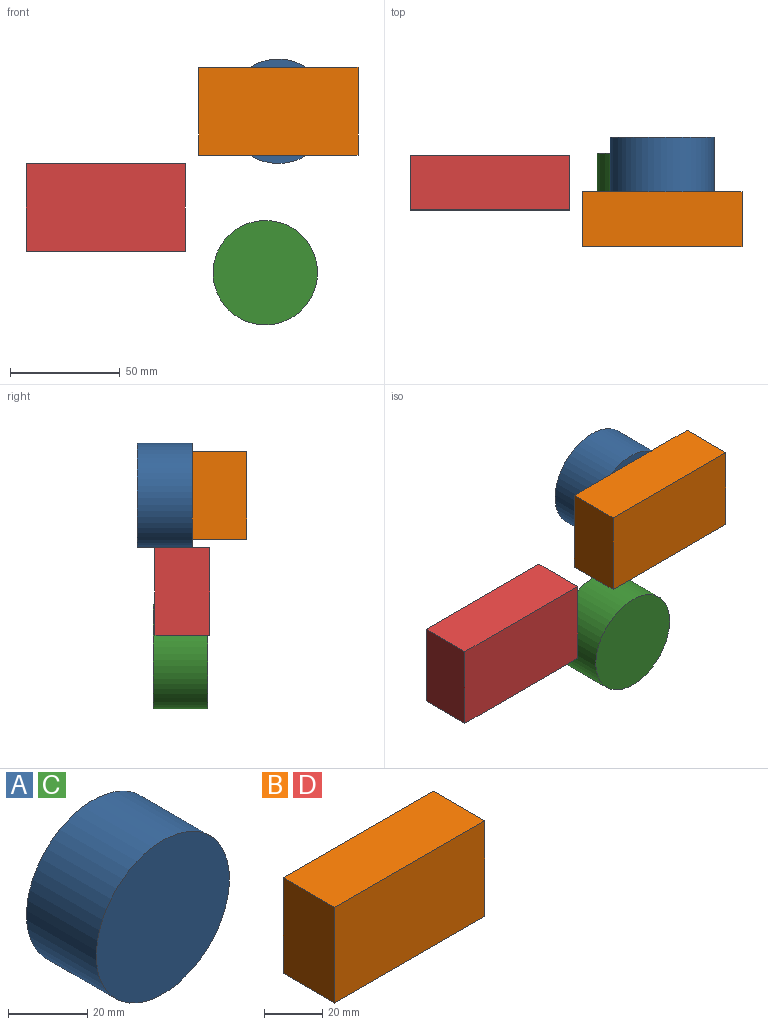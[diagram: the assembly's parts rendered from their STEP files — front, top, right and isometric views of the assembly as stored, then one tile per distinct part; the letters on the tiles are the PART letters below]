
ASSEMBLY  parts=4 mates=1
PART A: 3 faces, bbox 47.6x25x47.6 mm
  f0: cylinder r=23.79mm len=47.58mm, axis (0,1,0), area 3737.3mm2, adj f1,f2
  f1: plane 47.58x47.58mm, normal (0,-1,0), area 1778.3mm2, adj f0
  f2: plane 47.58x47.58mm, normal (0,1,0), area 1778.3mm2, adj f0
PART B: 6 faces, bbox 72.7x25x40 mm
  f0: plane 40.03x25mm, normal (-1,0,0), area 1000.7mm2, adj f1,f3,f4,f5
  f1: plane 72.71x25mm, normal (0,0,-1), area 1817.8mm2, adj f0,f2,f4,f5
  f2: plane 40.03x25mm, normal (1,0,0), area 1000.7mm2, adj f1,f3,f4,f5
  f3: plane 72.71x25mm, normal (0,0,1), area 1817.8mm2, adj f0,f2,f4,f5
  f4: plane 72.71x40.03mm, normal (0,-1,0), area 2910.6mm2, adj f0,f1,f2,f3
  f5: plane 72.71x40.03mm, normal (0,1,0), area 2910.6mm2, adj f0,f1,f2,f3
PART C: same geometry as A
PART D: same geometry as B
PLACE A t=(-65.49,8.13,45.03)mm fixed
PLACE B rot(axis=(1,0,0),180deg) t=(78.65,-41.87,122.03)mm
PLACE C t=(-71.4,0.89,-28.57)mm
PLACE D at identity
MATE revolute B.f4 <-> A.f0  axis (0,1,0) through (-25,-16.87,82.95)mm
